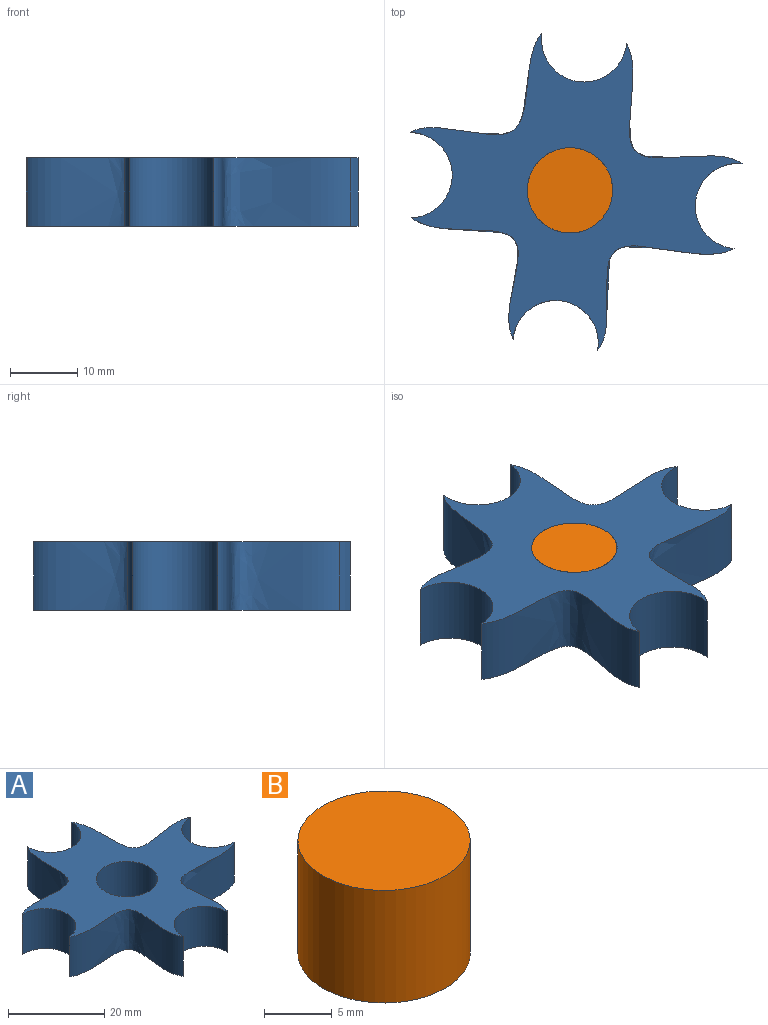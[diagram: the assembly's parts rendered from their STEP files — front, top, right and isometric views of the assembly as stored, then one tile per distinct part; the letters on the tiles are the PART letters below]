
ASSEMBLY  parts=2 mates=1
PART A: 11 faces, bbox 51.2x47.7x10.2 mm
  f0: extruded ~18.15x16.51mm, area 315.4mm2, adj f1,f7,f9,f10
  f1: cylinder r=6.35mm len=12.64mm, axis (0,0,-1), area 199mm2, adj f0,f2,f9,f10
  f2: extruded ~16.74x16.55mm, area 316.2mm2, adj f1,f3,f9,f10
  f3: cylinder r=6.35mm len=12.7mm, axis (0,0,-1), area 207.6mm2, adj f2,f4,f9,f10
  f4: extruded ~18.78x16.98mm, area 339.7mm2, adj f3,f5,f9,f10
  f5: cylinder r=6.35mm len=12.7mm, axis (0,0,-1), area 202.7mm2, adj f4,f6,f9,f10
  f6: extruded ~18.76x16.56mm, area 332.5mm2, adj f5,f7,f9,f10
  f7: cylinder r=6.35mm len=12.7mm, axis (0,0,-1), area 205.5mm2, adj f0,f6,f9,f10
  f8: cylinder r=6.35mm len=12.7mm, axis (0,0,-1), area 405.4mm2, adj f9,f10
  f9: plane 51.19x47.74mm, normal (0,0,1), area 780.9mm2, adj f0,f1,f2,f3,f4,f5,f6,f7
  f10: plane 51.19x47.74mm, normal (0,0,-1), area 780.9mm2, adj f0,f1,f2,f3,f4,f5,f6,f7
PART B: 3 faces, bbox 12.7x12.7x10.2 mm
  f0: cylinder r=6.35mm len=12.7mm, axis (0,0,-1), area 405.4mm2, adj f1,f2
  f1: plane 12.7x12.7mm, normal (0,0,1), area 126.7mm2, adj f0
  f2: plane 12.7x12.7mm, normal (0,0,-1), area 126.7mm2, adj f0
PLACE A rot(axis=(0,0,-1),5.4deg) t=(0,0,0)mm
PLACE B at identity fixed
MATE revolute B.f0 <-> A.f8  axis (0,0,-1) through (0,0,10.16)mm
